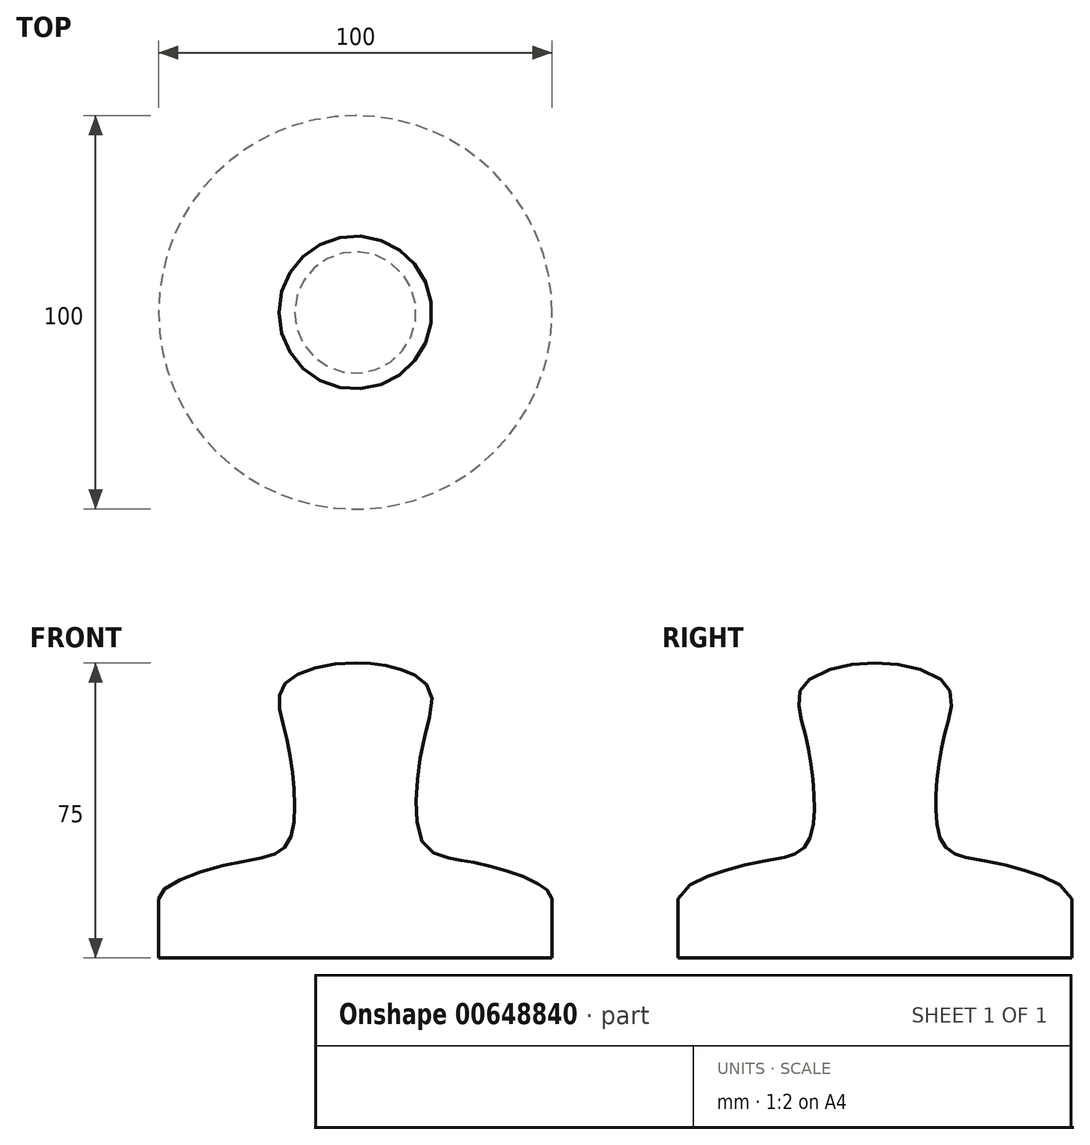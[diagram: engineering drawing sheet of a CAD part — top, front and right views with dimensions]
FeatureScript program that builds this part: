
annotation { "Feature Type Name" : "Feature", "Feature Type Description" : "" }
export const myFeature = defineFeature(function(context is Context, id is Id, definition is map)
    precondition{}
    {
        {
            var Q0;
            Q0=qCreatedBy(makeId("Front.planeOp"),FACE);
            var sketch = newSketch(context, id + "F0", { "sketchPlane" : qUnion([Q0])});
            skLineSegment(sketch, "E0", {"start": v(0, 0) * mm, "end": v(-50, 0) * mm});
            skLineSegment(sketch, "E1", {"start": v(-50, 0) * mm, "end": v(-50, 15) * mm});
            skFitSpline(sketch, "E2", {"points": [v(-50, 15) * mm, v(-31.35, 23.97) * mm, v(-17.9, 28.16) * mm, v(-15.46, 40.64) * mm, v(-17.77, 56.97) * mm, v(-18.39, 69.01) * mm, v(0, 75) * mm], "startDerivative": vector(0.05, 57.68) * mm, "endDerivative": vector(114.5, 0.1) * mm});
            skLineSegment(sketch, "E3", {"start": v(0, 0) * mm, "end": v(0, 75) * mm});
            skSolve(sketch);
        }
        {
            var Q0;
            Q0=makeQuery(id+"F0.imprint","IMPRINT",FACE,{"disambiguationData":[TD([[makeQuery(id+"F0.imprint","IMPRINT",EDGE,{"derivedFrom":sQuery(id+"F0.wireOp",EDGE,"E0")}),-1.0]])]});
            var Q1;
            Q1=sQuery(id+"F0.wireOp",EDGE,"E3");
            revolve(context, id + "F1", {"entities" : qUnion([Q0]), "axis" : qUnion([Q1]), "revolveType" : RevolveType.FULL});
        }
    });
